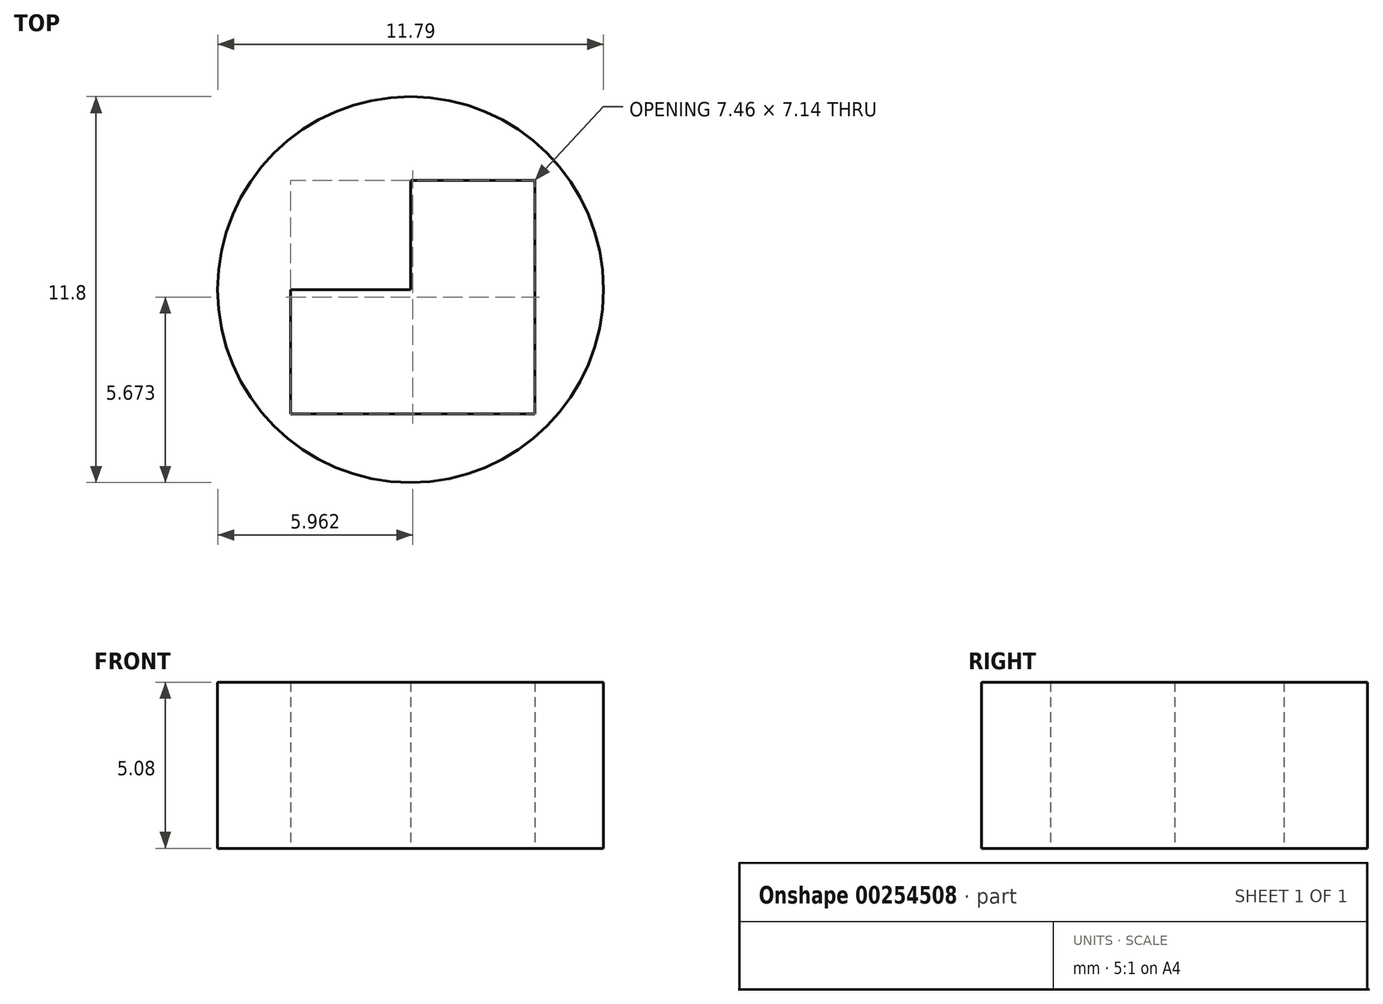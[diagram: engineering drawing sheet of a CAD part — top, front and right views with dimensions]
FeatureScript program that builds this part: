
annotation { "Feature Type Name" : "Feature", "Feature Type Description" : "" }
export const myFeature = defineFeature(function(context is Context, id is Id, definition is map)
    precondition{}
    {
        {
            var Q0;
            Q0=qCreatedBy(makeId("Top.planeOp"),FACE);
            var sketch = newSketch(context, id + "F0", { "sketchPlane" : qUnion([Q0])});
            skLineSegment(sketch, "E0", {"start": v(-33.45, 9.2) * mm, "end": v(-26.8, 16.12) * mm});
            skLineSegment(sketch, "E1", {"start": v(-26.8, 16.12) * mm, "end": v(-22.17, 16.12) * mm});
            skLineSegment(sketch, "E2", {"start": v(-22.17, 16.12) * mm, "end": v(-22.17, 19.99) * mm});
            skLineSegment(sketch, "E3", {"start": v(-22.17, 19.99) * mm, "end": v(-25.8, 19.97) * mm});
            skLineSegment(sketch, "E4", {"start": v(-25.8, 19.97) * mm, "end": v(-25.8, 38.73) * mm});
            skLineSegment(sketch, "E5", {"start": v(-25.8, 38.73) * mm, "end": v(-18.88, 45.9) * mm});
            skLineSegment(sketch, "E6", {"start": v(-18.88, 45.9) * mm, "end": v(14.3, 45.9) * mm});
            skLineSegment(sketch, "E7", {"start": v(14.3, 45.9) * mm, "end": v(22.2, 38.73) * mm});
            skLineSegment(sketch, "E8", {"start": v(22.2, 38.73) * mm, "end": v(22.2, 19.97) * mm});
            skLineSegment(sketch, "E9", {"start": v(22.2, 19.97) * mm, "end": v(18.52, 19.97) * mm});
            skLineSegment(sketch, "E10", {"start": v(18.52, 19.97) * mm, "end": v(18.52, 16.12) * mm});
            skLineSegment(sketch, "E11", {"start": v(18.52, 16.12) * mm, "end": v(22.2, 16.12) * mm});
            skLineSegment(sketch, "E12", {"start": v(22.2, 16.12) * mm, "end": v(29.83, 9.43) * mm});
            skLineSegment(sketch, "E13", {"start": v(29.83, 9.43) * mm, "end": v(29.83, -20.85) * mm});
            skLineSegment(sketch, "E14", {"start": v(29.83, -20.85) * mm, "end": v(22.14, -20.85) * mm});
            skLineSegment(sketch, "E15", {"start": v(22.14, -20.85) * mm, "end": v(22.14, -32.04) * mm});
            skLineSegment(sketch, "E16", {"start": v(22.14, -32.04) * mm, "end": v(19.03, -35.7) * mm});
            skLineSegment(sketch, "E17", {"start": v(19.03, -35.7) * mm, "end": v(3.87, -35.7) * mm});
            skLineSegment(sketch, "E18", {"start": v(3.87, -35.7) * mm, "end": v(3.87, -28.47) * mm});
            skLineSegment(sketch, "E19", {"start": v(3.87, -28.47) * mm, "end": v(-7.29, -28.47) * mm});
            skLineSegment(sketch, "E20", {"start": v(-7.29, -28.47) * mm, "end": v(-7.29, -35.7) * mm});
            skLineSegment(sketch, "E21", {"start": v(-7.29, -35.7) * mm, "end": v(-23.05, -35.7) * mm});
            skLineSegment(sketch, "E22", {"start": v(-23.05, -35.7) * mm, "end": v(-25.8, -32.44) * mm});
            skLineSegment(sketch, "E23", {"start": v(-25.8, -32.44) * mm, "end": v(-25.8, -20.85) * mm});
            skLineSegment(sketch, "E24", {"start": v(-25.8, -20.85) * mm, "end": v(-33.32, -20.85) * mm});
            skLineSegment(sketch, "E25", {"start": v(-33.32, -20.85) * mm, "end": v(-33.45, 9.2) * mm});
            skCircle(sketch, "E26", {"center": v(-11.3, 31.23) * mm, "radius": 5.9 * mm});
            skPoint(sketch, "E26.first.point", {"position": v(-17.19, 30.94) * mm});
            skPoint(sketch, "E26.second.point", {"position": v(-5.4, 31.07) * mm});
            skPoint(sketch, "E26.third.point", {"position": v(-11.26, 25.33) * mm});
            skCircle(sketch, "E27", {"center": v(7.12, 31) * mm, "radius": 5.64 * mm});
            skPoint(sketch, "E27.first.point", {"position": v(1.48, 30.84) * mm});
            skPoint(sketch, "E27.second.point", {"position": v(12.76, 30.78) * mm});
            skPoint(sketch, "E27.third.point", {"position": v(7.1, 36.64) * mm});
            skLineSegment(sketch, "E28.bottom", {"start": v(-14.96, 34.57) * mm, "end": v(-7.5, 34.57) * mm});
            skLineSegment(sketch, "E28.top", {"start": v(-14.96, 27.44) * mm, "end": v(-7.5, 27.44) * mm});
            skLineSegment(sketch, "E28.left", {"start": v(-14.96, 34.57) * mm, "end": v(-14.96, 27.44) * mm});
            skLineSegment(sketch, "E28.right", {"start": v(-7.5, 34.57) * mm, "end": v(-7.5, 27.44) * mm});
            skLineSegment(sketch, "E29.bottom", {"start": v(3.8, 34.28) * mm, "end": v(10.72, 34.28) * mm});
            skLineSegment(sketch, "E29.top", {"start": v(3.8, 27.44) * mm, "end": v(10.72, 27.44) * mm});
            skLineSegment(sketch, "E29.left", {"start": v(3.8, 34.28) * mm, "end": v(3.8, 27.44) * mm});
            skLineSegment(sketch, "E29.right", {"start": v(10.72, 34.28) * mm, "end": v(10.72, 27.44) * mm});
            skLineSegment(sketch, "E30.bottom", {"start": v(7.12, 31) * mm, "end": v(3.8, 31) * mm});
            skLineSegment(sketch, "E30.top", {"start": v(7.12, 34.28) * mm, "end": v(3.8, 34.28) * mm});
            skLineSegment(sketch, "E30.left", {"start": v(7.12, 31) * mm, "end": v(7.12, 34.28) * mm});
            skLineSegment(sketch, "E30.right", {"start": v(3.8, 31) * mm, "end": v(3.8, 34.28) * mm});
            skLineSegment(sketch, "E31.bottom", {"start": v(-11.3, 31.23) * mm, "end": v(-14.96, 31.23) * mm});
            skLineSegment(sketch, "E31.top", {"start": v(-11.3, 34.57) * mm, "end": v(-14.96, 34.57) * mm});
            skLineSegment(sketch, "E31.left", {"start": v(-11.3, 31.23) * mm, "end": v(-11.3, 34.57) * mm});
            skLineSegment(sketch, "E31.right", {"start": v(-14.96, 31.23) * mm, "end": v(-14.96, 34.57) * mm});
            skLineSegment(sketch, "E32.bottom", {"start": v(-3.8, 23.6) * mm, "end": v(0, 23.6) * mm});
            skLineSegment(sketch, "E32.top", {"start": v(-3.8, 19.8) * mm, "end": v(0, 19.8) * mm});
            skLineSegment(sketch, "E32.left", {"start": v(-3.8, 23.6) * mm, "end": v(-3.8, 19.8) * mm});
            skLineSegment(sketch, "E32.right", {"start": v(0, 23.6) * mm, "end": v(0, 19.8) * mm});
            skLineSegment(sketch, "E33.bottom", {"start": v(-7.5, 15.86) * mm, "end": v(3.8, 15.86) * mm});
            skLineSegment(sketch, "E33.top", {"start": v(-7.5, 12.27) * mm, "end": v(3.8, 12.27) * mm});
            skLineSegment(sketch, "E33.left", {"start": v(-7.5, 15.86) * mm, "end": v(-7.5, 12.27) * mm});
            skLineSegment(sketch, "E33.right", {"start": v(3.8, 15.86) * mm, "end": v(3.8, 12.27) * mm});
            skPoint(sketch, "E34.oppositeSnap0", {"position": v(-25.8, -26.64) * mm});
            skLineSegment(sketch, "E34.bottom", {"start": v(-29.45, -9.9) * mm, "end": v(-25.8, -9.9) * mm});
            skLineSegment(sketch, "E34.top", {"start": v(-29.45, -17.27) * mm, "end": v(-25.8, -17.27) * mm});
            skLineSegment(sketch, "E34.left", {"start": v(-29.45, -9.9) * mm, "end": v(-29.45, -17.27) * mm});
            skLineSegment(sketch, "E34.right", {"start": v(-25.8, -9.9) * mm, "end": v(-25.8, -17.27) * mm});
            skLineSegment(sketch, "E35.top", {"start": v(-29.45, 8.74) * mm, "end": v(-25.8, 8.74) * mm});
            skLineSegment(sketch, "E35.left", {"start": v(-29.45, -9.9) * mm, "end": v(-29.45, 8.74) * mm});
            skLineSegment(sketch, "E35.right", {"start": v(-25.8, -9.9) * mm, "end": v(-25.8, 8.74) * mm});
            skLineSegment(sketch, "E36.bottom", {"start": v(22.2, -9.9) * mm, "end": v(25.76, -9.9) * mm});
            skLineSegment(sketch, "E36.top", {"start": v(22.2, -17.27) * mm, "end": v(25.76, -17.27) * mm});
            skLineSegment(sketch, "E36.left", {"start": v(22.2, -9.9) * mm, "end": v(22.2, -17.27) * mm});
            skLineSegment(sketch, "E36.right", {"start": v(25.76, -9.9) * mm, "end": v(25.76, -17.27) * mm});
            skLineSegment(sketch, "E37.top", {"start": v(22.2, 8.7) * mm, "end": v(25.76, 8.7) * mm});
            skLineSegment(sketch, "E37.left", {"start": v(22.2, -9.9) * mm, "end": v(22.2, 8.7) * mm});
            skLineSegment(sketch, "E37.right", {"start": v(25.76, -9.9) * mm, "end": v(25.76, 8.7) * mm});
            skLineSegment(sketch, "E38.bottom", {"start": v(-3.6, -28.47) * mm, "end": v(0, -28.47) * mm});
            skLineSegment(sketch, "E38.top", {"start": v(-3.6, -24.74) * mm, "end": v(0, -24.74) * mm});
            skLineSegment(sketch, "E38.left", {"start": v(-3.6, -28.47) * mm, "end": v(-3.6, -24.74) * mm});
            skLineSegment(sketch, "E38.right", {"start": v(0, -28.47) * mm, "end": v(0, -24.74) * mm});
            skLineSegment(sketch, "E39", {"start": v(-22.24, -24.61) * mm, "end": v(-22.24, -31.85) * mm});
            skLineSegment(sketch, "E40", {"start": v(-22.24, -31.85) * mm, "end": v(-11.06, -31.85) * mm});
            skLineSegment(sketch, "E41", {"start": v(-11.06, -31.85) * mm, "end": v(-11.06, -28.48) * mm});
            skLineSegment(sketch, "E42", {"start": v(-11.06, -28.48) * mm, "end": v(-7.29, -28.47) * mm});
            skLineSegment(sketch, "E43", {"start": v(-7.29, -24.61) * mm, "end": v(-22.24, -24.61) * mm});
            skLineSegment(sketch, "E44", {"start": v(-7.29, -24.61) * mm, "end": v(-7.29, -28.47) * mm});
            skLineSegment(sketch, "E45", {"start": v(3.87, -28.47) * mm, "end": v(3.87, -24.61) * mm});
            skLineSegment(sketch, "E46", {"start": v(3.87, -24.61) * mm, "end": v(18.56, -24.61) * mm});
            skLineSegment(sketch, "E47", {"start": v(18.56, -24.61) * mm, "end": v(18.56, -31.97) * mm});
            skLineSegment(sketch, "E48", {"start": v(18.56, -31.97) * mm, "end": v(7.4, -31.97) * mm});
            skLineSegment(sketch, "E49", {"start": v(7.4, -31.97) * mm, "end": v(7.4, -28.47) * mm});
            skLineSegment(sketch, "E50", {"start": v(7.4, -28.47) * mm, "end": v(3.87, -28.47) * mm});
            skLineSegment(sketch, "E51", {"start": v(-22.17, 19.99) * mm, "end": v(-22.24, 38.23) * mm});
            skLineSegment(sketch, "E52", {"start": v(-22.24, 38.23) * mm, "end": v(-18.48, 38.25) * mm});
            skLineSegment(sketch, "E53", {"start": v(-18.48, 38.25) * mm, "end": v(-18.5, 42.04) * mm});
            skLineSegment(sketch, "E54", {"start": v(-18.5, 42.04) * mm, "end": v(14.76, 42.16) * mm});
            skLineSegment(sketch, "E55", {"start": v(14.76, 42.16) * mm, "end": v(14.78, 38.23) * mm});
            skLineSegment(sketch, "E56", {"start": v(14.78, 38.23) * mm, "end": v(18.52, 38.24) * mm});
            skLineSegment(sketch, "E57", {"start": v(18.52, 38.24) * mm, "end": v(18.52, 19.97) * mm});
            skLineSegment(sketch, "E58", {"start": v(3.8, 15.86) * mm, "end": v(3.8, 19.97) * mm});
            skLineSegment(sketch, "E59", {"start": v(3.8, 19.97) * mm, "end": v(18.52, 19.97) * mm});
            skLineSegment(sketch, "E60", {"start": v(-7.5, 15.86) * mm, "end": v(-7.5, 19.99) * mm});
            skLineSegment(sketch, "E61", {"start": v(-7.5, 19.99) * mm, "end": v(-22.17, 19.99) * mm});
            skLineSegment(sketch, "E62", {"start": v(-22.23, 12.38) * mm, "end": v(-22.23, -21.38) * mm});
            skLineSegment(sketch, "E63", {"start": v(-22.23, -21.38) * mm, "end": v(18.48, -21.38) * mm});
            skLineSegment(sketch, "E64", {"start": v(18.48, -21.38) * mm, "end": v(18.48, 12.34) * mm});
            skLineSegment(sketch, "E65", {"start": v(18.48, 12.34) * mm, "end": v(14.65, 12.34) * mm});
            skLineSegment(sketch, "E66", {"start": v(14.65, 12.34) * mm, "end": v(14.65, 15.86) * mm});
            skLineSegment(sketch, "E67", {"start": v(14.65, 15.86) * mm, "end": v(3.8, 15.86) * mm});
            skLineSegment(sketch, "E68", {"start": v(-22.23, 12.38) * mm, "end": v(-18.53, 12.38) * mm});
            skLineSegment(sketch, "E69", {"start": v(-18.53, 12.38) * mm, "end": v(-18.53, 15.86) * mm});
            skLineSegment(sketch, "E70", {"start": v(-18.53, 15.86) * mm, "end": v(-7.5, 15.86) * mm});
            skLineSegment(sketch, "E71.bottom", {"start": v(-7.42, -28.31) * mm, "end": v(-7.13, -28.31) * mm});
            skLineSegment(sketch, "E71.top", {"start": v(-7.42, -28.63) * mm, "end": v(-7.13, -28.63) * mm});
            skLineSegment(sketch, "E71.left", {"start": v(-7.42, -28.31) * mm, "end": v(-7.42, -28.63) * mm});
            skLineSegment(sketch, "E71.right", {"start": v(-7.13, -28.31) * mm, "end": v(-7.13, -28.63) * mm});
            skLineSegment(sketch, "E72.bottom", {"start": v(3.95, -28.38) * mm, "end": v(3.78, -28.38) * mm});
            skLineSegment(sketch, "E72.top", {"start": v(3.95, -28.56) * mm, "end": v(3.78, -28.56) * mm});
            skLineSegment(sketch, "E72.left", {"start": v(3.95, -28.38) * mm, "end": v(3.95, -28.56) * mm});
            skLineSegment(sketch, "E72.right", {"start": v(3.78, -28.38) * mm, "end": v(3.78, -28.56) * mm});
            skSolve(sketch);
        }
        {
            var Q0;
            Q0=makeQuery(id+"F0.imprint","IMPRINT",FACE,{"disambiguationData":[TD([[makeQuery(id+"F0.imprint","IMPRINT",EDGE,{"derivedFrom":sQuery(id+"F0.wireOp",EDGE,"E26")}),1.0]])]});
            var Q1;
            Q1=makeQuery(id+"F0.imprint","IMPRINT",FACE,{"disambiguationData":[TD([[makeQuery(id+"F0.imprint","IMPRINT",EDGE,{"derivedFrom":sQuery(id+"F0.wireOp",EDGE,"E31.bottom")}),-1.0]])]});
            var Q2;
            Q2=makeQuery(id+"F0.imprint","IMPRINT",FACE,{"disambiguationData":[TD([[makeQuery(id+"F0.imprint","IMPRINT",EDGE,{"derivedFrom":sQuery(id+"F0.wireOp",EDGE,"E28.bottom")}),-1.0]])]});
            extrude(context, id + "F1", {"entities" : qUnion([Q0, Q1, Q2]), "depth" : 5.08 * mm});
        }
    });
